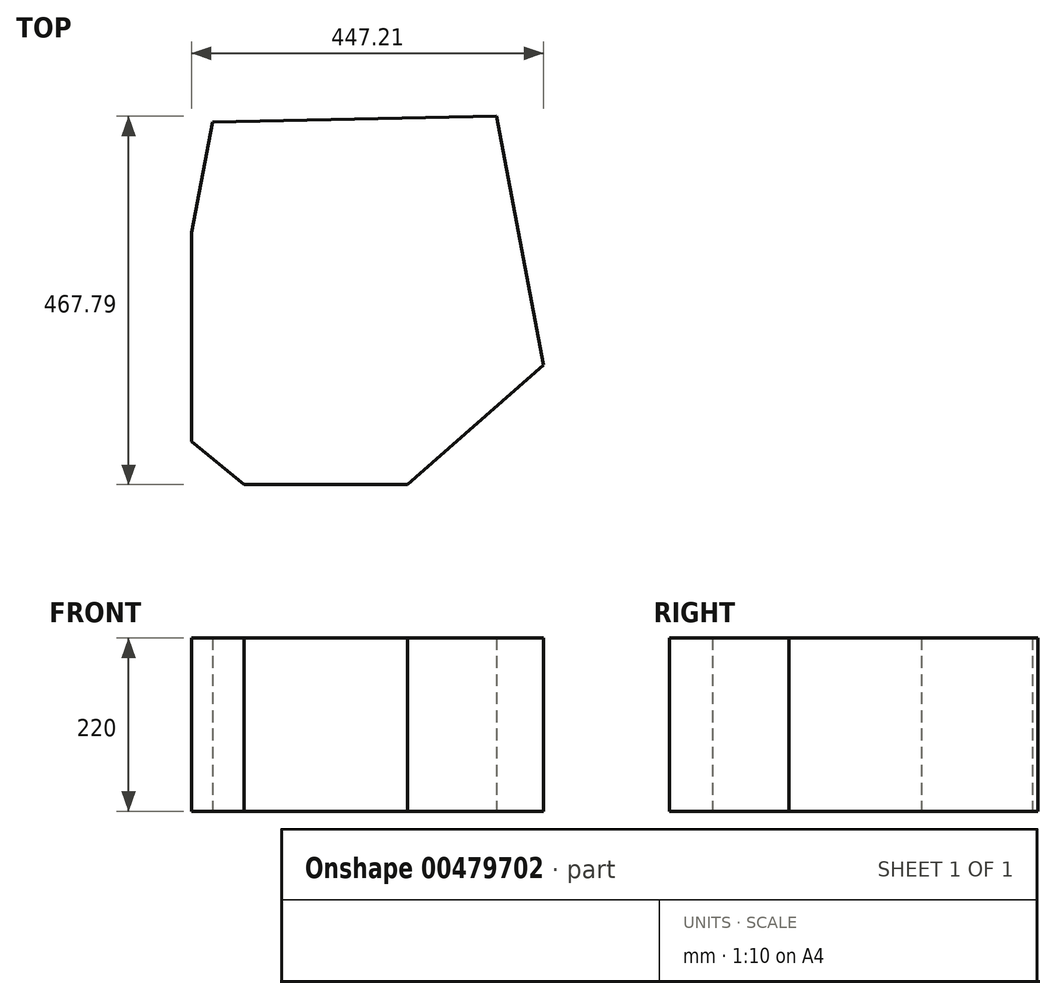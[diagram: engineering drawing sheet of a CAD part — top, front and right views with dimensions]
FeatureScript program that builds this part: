
annotation { "Feature Type Name" : "Feature", "Feature Type Description" : "" }
export const myFeature = defineFeature(function(context is Context, id is Id, definition is map)
    precondition{}
    {
        {
            var Q0;
            Q0=qCreatedBy(makeId("Top.planeOp"),FACE);
            var sketch = newSketch(context, id + "F0", { "sketchPlane" : qUnion([Q0])});
            skLineSegment(sketch, "E0", {"start": v(-193.4, 279.5) * mm, "end": v(167.33, 286.6) * mm});
            skLineSegment(sketch, "E1", {"start": v(167.33, 286.6) * mm, "end": v(227.43, -29.44) * mm});
            skLineSegment(sketch, "E2", {"start": v(227.43, -29.44) * mm, "end": v(54.37, -181.19) * mm});
            skLineSegment(sketch, "E3", {"start": v(54.37, -181.19) * mm, "end": v(-153.35, -181.19) * mm});
            skLineSegment(sketch, "E4", {"start": v(-153.35, -181.19) * mm, "end": v(-219.78, -126.58) * mm});
            skLineSegment(sketch, "E5", {"start": v(-219.78, -126.58) * mm, "end": v(-219.78, 138.85) * mm});
            skLineSegment(sketch, "E6", {"start": v(-219.78, 138.85) * mm, "end": v(-193.4, 279.5) * mm});
            skSolve(sketch);
        }
        {
            var Q0;
            Q0=qSketchRegion(id+"F0",true);
            extrude(context, id + "F1", {"entities" : qUnion([Q0]), "depth" : 220 * mm});
        }
    });
